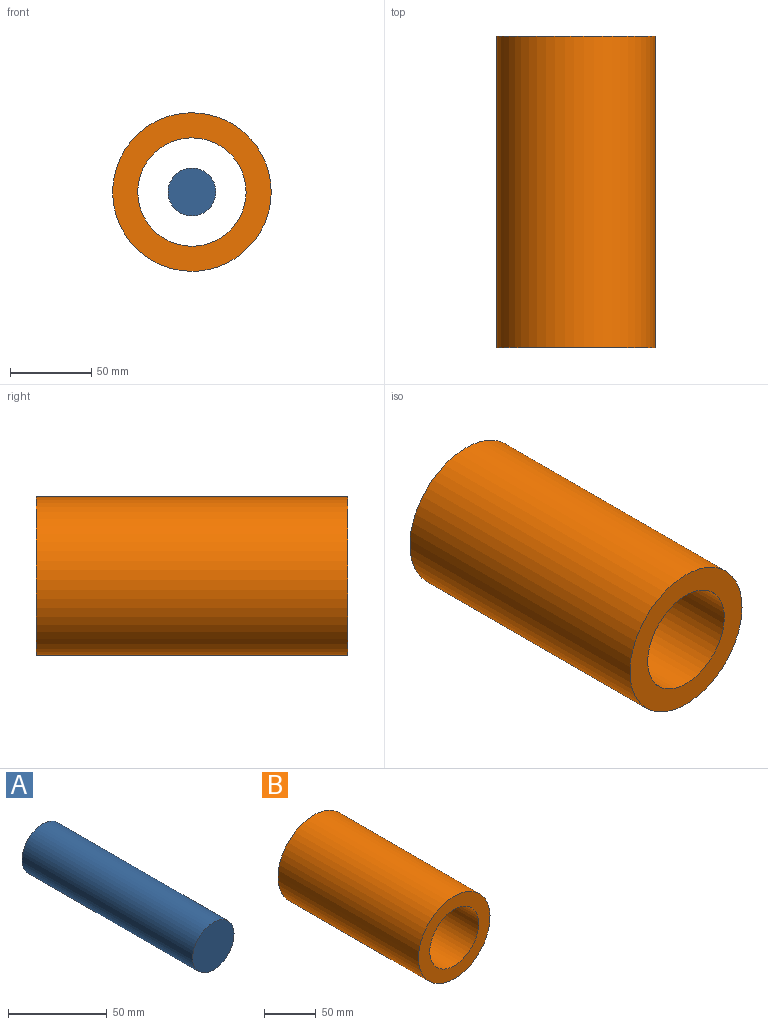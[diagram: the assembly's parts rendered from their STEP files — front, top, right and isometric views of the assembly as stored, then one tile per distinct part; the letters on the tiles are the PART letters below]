
ASSEMBLY  parts=2 mates=1
PART A: 3 faces, bbox 29.6x122x29.6 mm
  f0: cylinder r=14.79mm len=122mm, axis (0,1,0), area 11333.7mm2, adj f1,f2
  f1: plane 29.57x29.57mm, normal (0,-1,0), area 686.8mm2, adj f0
  f2: plane 29.57x29.57mm, normal (0,1,0), area 686.8mm2, adj f0
PART B: 4 faces, bbox 97.8x192x97.8 mm
  f0: cylinder r=33.41mm len=192mm, axis (0,-1,0), area 40310.1mm2, adj f2,f3
  f1: cylinder r=48.91mm len=192mm, axis (0,-1,0), area 58999.1mm2, adj f2,f3
  f2: plane 97.81x97.81mm, normal (0,1,0), area 4006.5mm2, adj f0,f1
  f3: plane 97.81x97.81mm, normal (0,-1,0), area 4006.5mm2, adj f0,f1
PLACE A t=(76.11,60.41,52.27)mm fixed
PLACE B rot(axis=(0,1,0),101.2deg) t=(76.11,-96.44,52.27)mm
MATE cylindrical B.f0 <-> A.f0  axis (0,-1,0) through (76.11,-0.44,52.27)mm
